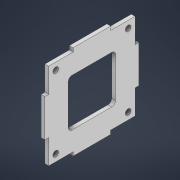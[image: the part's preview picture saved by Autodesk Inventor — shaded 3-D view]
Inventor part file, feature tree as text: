
AUTODESK INVENTOR PART (.ipt)
format: ipt  version: 2022 (Build 260153000, 153)  size: 186,880 bytes
history: native  units: in
note: dims shown in document units (in); Inventor stores cm internally (conversion verified against a paired STEP export)
features: sketch x7, hole x4, extrude x3
ambient origin geometry x8: Origin, YZ Plane, XZ Plane, XY Plane, X Axis, Y Axis, Z Axis, Center Point
bodies: Solid1 (feature_tree)
feature tree (14):
  extrude  "Extrusion1"  Depth=1.9685in
  hole  "Hole1"  [1 undecoded]
  hole  "Hole2"  [1 undecoded]
  hole  "Hole3"  [1 undecoded]
  hole  "Hole4"  [1 undecoded]
  extrude  "Extrusion3"  Depth=0.0787in
  extrude  "Extrusion4"  Depth=0.0787in
  sketch  "Sketch1"  dims[d0=1.9685in d1=1.9685in]
  sketch  "Sketch3"  dims[d2=1.8898in d3=1.8898in]
  sketch  "Sketch4"  dims[d4=0.0787in d5=0.0in d6=1.5197in]
  sketch  "Sketch5"  dims[d7=1.5197in d8=0.1181in]
  sketch  "Sketch6"  dims[d9=0.1225in d10=0.1225in]
  sketch  "Sketch7"  dims[d11=0.1225in]
  sketch  "Sketch9"  dims[d12=0.1181in d13=0.2362in d14=0.1575in d15=0.0787in d16=90.0deg d17=0.315in d18=0.8108in d19=1.5197in d20=1.5197in d21=0.1181in d22=0.1181in d23=0.2362in d24=0.1575in d25=0.0787in d26=90.0deg d27=0.315in d28=0.8108in d29=1.5197in d30=1.5197in d31=0.1181in d32=0.1181in d33=0.2362in d34=0.1575in d35=0.0787in d36=90.0deg d37=0.315in d38=0.8108in d39=1.5197in d40=1.5197in d41=0.1181in d42=0.1181in d43=0.2362in d44=0.1575in d45=0.0787in d46=90.0deg d47=0.315in d48=0.8108in d49=1.811in d50=1.811in d51=0.7874in d52=0.7874in d53=0.7874in d54=0.7874in d57=0.0787in d58=0.0in d62=0.9921in d63=0.9921in d64=0.0787in d65=0.0787in d66=0.0in d55=0.5635in d56=0.0295in d59=0.0295in d60=0.0148in]
note: 4 required parameter values undecoded (feature->parameter linkage not recoverable at this tier; creation-order binding heuristic only, values carry confidence <= 0.55)
